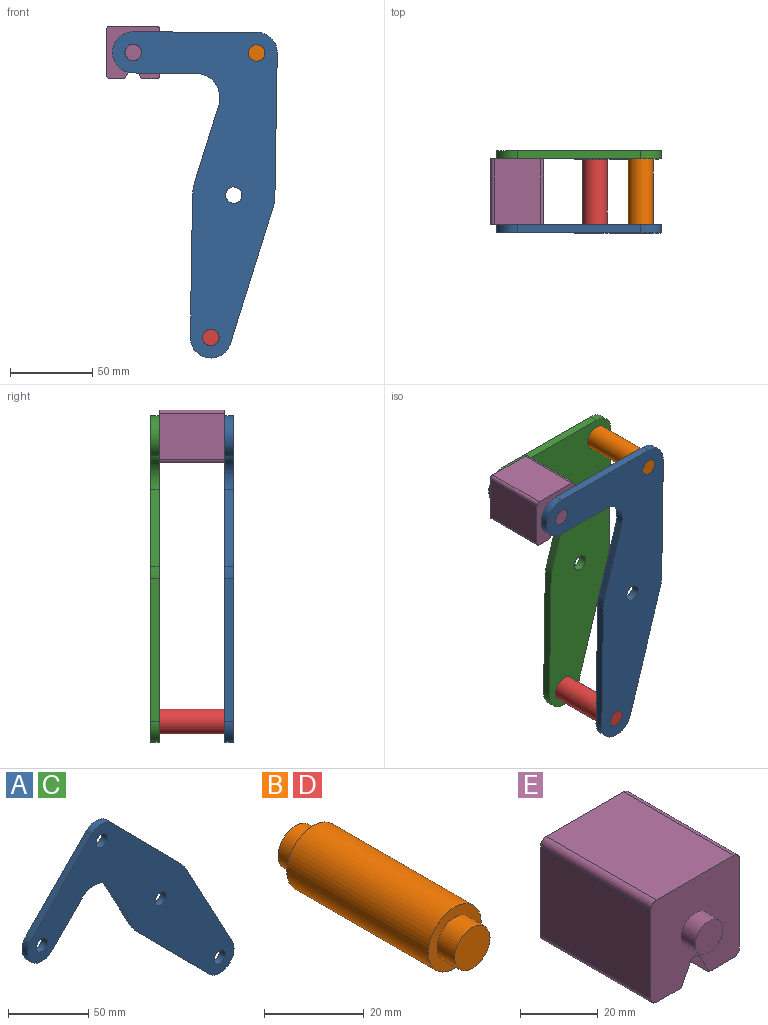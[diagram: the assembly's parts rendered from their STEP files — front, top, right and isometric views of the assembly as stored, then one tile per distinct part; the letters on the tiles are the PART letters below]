
ASSEMBLY  parts=5 mates=3
PART A: 18 faces, bbox 181.7x5x165.8 mm
  f0: plane 43.49x23.35mm, normal (-0.88,0,-0.47), area 246.8mm2, adj f1,f14,f16,f17
  f1: cylinder r=25mm len=5.75mm, axis (0,1,0), area 35.8mm2, adj f0,f2,f16,f17
  f2: plane 61.6x60.87mm, normal (-0.71,0,-0.7), area 433mm2, adj f1,f3,f16,f17
  f3: cylinder r=12.5mm len=21.39mm, axis (0,1,0), area 178.4mm2, adj f2,f4,f16,f17
  f4: plane 76.3x40.96mm, normal (0.88,0,0.47), area 433mm2, adj f3,f5,f16,f17
  f5: cylinder r=25mm len=5.75mm, axis (0,1,0), area 35.8mm2, adj f4,f6,f16,f17
  f6: plane 61.6x60.87mm, normal (0.71,0,0.7), area 433mm2, adj f5,f7,f16,f17
  f7: cylinder r=12.5mm len=17.78mm, axis (0,1,0), area 98.9mm2, adj f6,f8,f16,f17
  f8: plane 53.35x52.71mm, normal (-0.71,0,0.7), area 375mm2, adj f7,f9,f16,f17
  f9: cylinder r=12.5mm len=21.39mm, axis (0,1,0), area 196.3mm2, adj f8,f10,f16,f17
  f10: plane 26.86x26.54mm, normal (0.71,0,-0.7), area 188.8mm2, adj f9,f14,f16,f17
  f11: cylinder r=5mm len=10mm, axis (0,1,0), area 157.1mm2, adj f16,f17
  f12: cylinder r=5mm len=10mm, axis (0,1,0), area 157.1mm2, adj f16,f17
  f13: cylinder r=5mm len=10mm, axis (0,1,0), area 157.1mm2, adj f16,f17
  f14: cylinder r=15mm len=23.89mm, axis (0,1,0), area 140.2mm2, adj f0,f10,f16,f17
  f15: cylinder r=5mm len=10mm, axis (0,1,0), area 157.1mm2, adj f16,f17
  f16: plane 181.66x165.78mm, normal (0,-1,0), area 8710.1mm2, adj f0,f1,f2,f3,f4,f5,f6,f7
  f17: plane 181.66x165.78mm, normal (0,1,0), area 8710.1mm2, adj f0,f1,f2,f3,f4,f5,f6,f7
PART B: 7 faces, bbox 15x50x15 mm
  f0: cylinder r=7.5mm len=40mm, axis (0,-1,0), area 1885mm2, adj f2,f5
  f1: cylinder r=5mm len=10mm, axis (0,1,0), area 157.1mm2, adj f2,f3
  f2: plane 15x15mm, normal (0,-1,0), area 98.2mm2, adj f0,f1
  f3: plane 10x10mm, normal (0,-1,0), area 78.5mm2, adj f1
  f4: cylinder r=5mm len=10mm, axis (0,-1,0), area 157.1mm2, adj f5,f6
  f5: plane 15x15mm, normal (0,1,0), area 98.2mm2, adj f0,f4
  f6: plane 10x10mm, normal (0,1,0), area 78.5mm2, adj f4
PART C: same geometry as A
PART D: same geometry as B
PART E: 18 faces, bbox 32.1x50x32.1 mm
  f0: plane 40x28.08mm, normal (1,0,0), area 1123.1mm2, adj f4,f10,f13,f14
  f1: plane 40x9.04mm, normal (0,0,-1), area 361.6mm2, adj f2,f4,f10,f14
  f2: plane 40x6.42mm, normal (-0.89,0,-0.45), area 287.2mm2, adj f1,f4,f10,f15
  f3: plane 40x6.42mm, normal (0.89,0,-0.45), area 287.2mm2, adj f4,f5,f10,f15
  f4: plane 32.08x32.08mm, normal (0,-1,0), area 900.6mm2, adj f0,f1,f2,f3,f5,f6,f7,f9
  f5: plane 40x9.04mm, normal (0,0,-1), area 361.6mm2, adj f3,f4,f10,f16
  f6: plane 40x28.08mm, normal (0,0,1), area 1123.1mm2, adj f4,f10,f13,f17
  f7: plane 40x28.08mm, normal (-1,0,0), area 1123.1mm2, adj f4,f10,f16,f17
  f8: plane 10x10mm, normal (0,-1,0), area 78.5mm2, adj f9
  f9: cylinder r=5mm len=10mm, axis (0,1,0), area 157.1mm2, adj f4,f8
  f10: plane 32.08x32.08mm, normal (0,1,0), area 900.6mm2, adj f0,f1,f2,f3,f5,f6,f7,f12
  f11: plane 10x10mm, normal (0,1,0), area 78.5mm2, adj f12
  f12: cylinder r=5mm len=10mm, axis (0,-1,0), area 157.1mm2, adj f10,f11
  f13: cylinder r=2mm len=40mm, axis (0,1,0), area 125.7mm2, adj f0,f4,f6,f10
  f14: cylinder r=2mm len=40mm, axis (0,-1,0), area 125.7mm2, adj f0,f1,f4,f10
  f15: cylinder r=2mm len=40mm, axis (0,1,0), area 177.1mm2, adj f2,f3,f4,f10
  f16: cylinder r=2mm len=40mm, axis (0,1,0), area 125.7mm2, adj f4,f5,f7,f10
  f17: cylinder r=2mm len=40mm, axis (0,-1,0), area 125.7mm2, adj f4,f6,f7,f10
PLACE A rot(axis=(0,1,0),45.6deg) t=(0,-20,0)mm fixed
PLACE B rot(axis=(0,1,0),45.6deg) t=(0,-20,0)mm
PLACE C rot(axis=(0,1,0),45.6deg) t=(0,25,0)mm
PLACE D rot(axis=(0,-1,0),44.4deg) t=(72.47,-20,-100.3)mm
PLACE E t=(43.6,-20,69.67)mm
MATE revolute E.f9 <-> A.f9  axis (0,-1,0) through (-61.08,-25,86.71)mm
MATE fastened B.f0 <-> C.f7  axis (0,1,0) through (13.92,25,86.39)mm
MATE fastened D.f0 <-> C.f3  axis (0,1,0) through (-13.92,25,-86.39)mm
